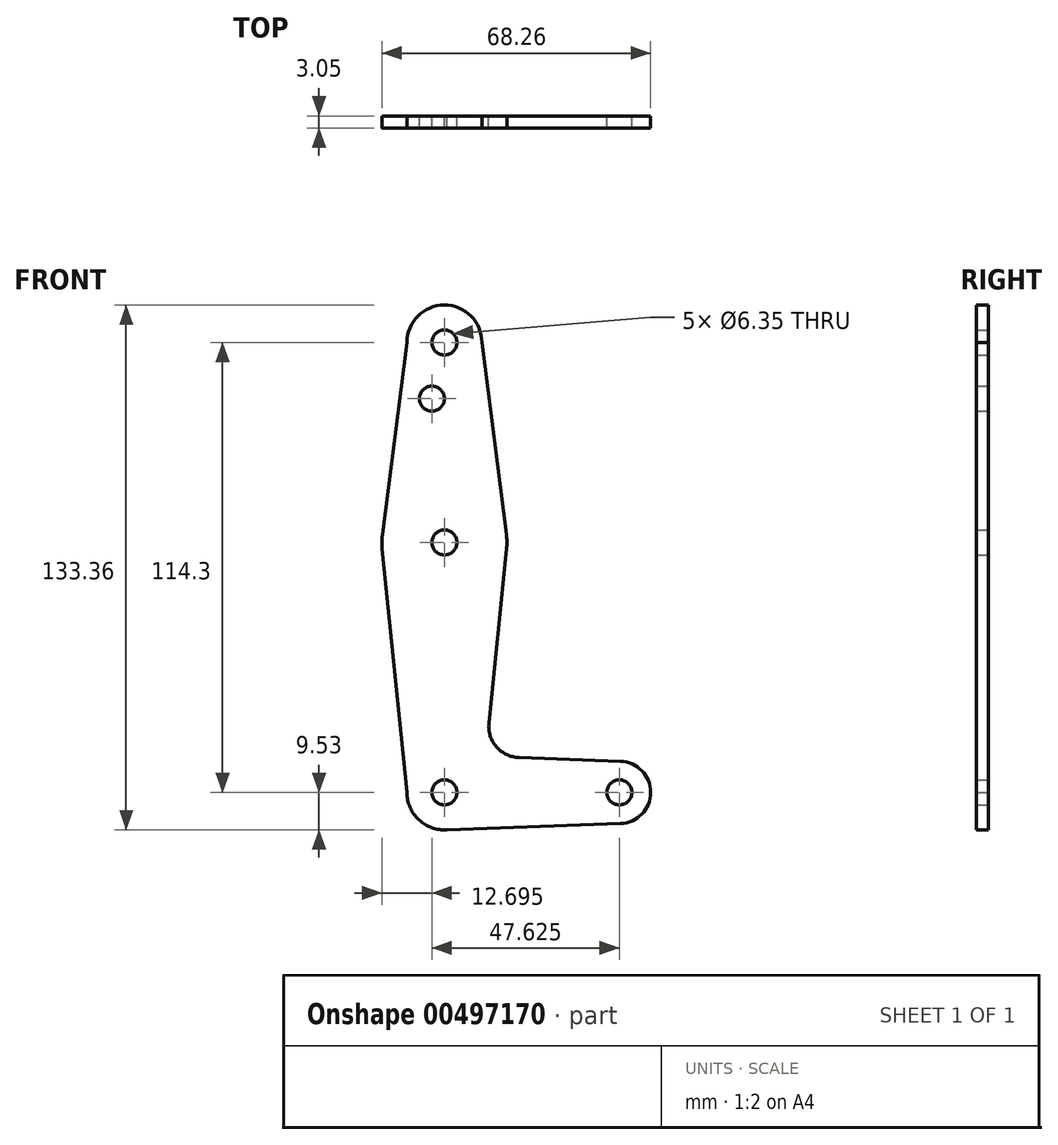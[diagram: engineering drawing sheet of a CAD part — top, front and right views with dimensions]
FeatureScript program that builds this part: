
annotation { "Feature Type Name" : "Feature", "Feature Type Description" : "" }
export const myFeature = defineFeature(function(context is Context, id is Id, definition is map)
    precondition{}
    {
        {
            var Q0;
            Q0=qCreatedBy(makeId("Front.planeOp"),FACE);
            var sketch = newSketch(context, id + "F0", { "sketchPlane" : qUnion([Q0])});
            skLineSegment(sketch, "E0", {"start": v(0, 0) * mm, "end": v(0, 114.3) * mm, "construction": true});
            skLineSegment(sketch, "E1", {"start": v(0, 0) * mm, "end": v(44.45, 0) * mm, "construction": true});
            skCircle(sketch, "E2", {"center": v(0, 0) * mm, "radius": 9.53 * mm});
            skCircle(sketch, "E3", {"center": v(44.45, 0) * mm, "radius": 7.94 * mm});
            skCircle(sketch, "E4", {"center": v(0, 63.5) * mm, "radius": 15.88 * mm});
            skCircle(sketch, "E5", {"center": v(0, 114.3) * mm, "radius": 9.53 * mm});
            skLineSegment(sketch, "E6", {"start": v(9.53, 114.3) * mm, "end": v(15.75, 65.5) * mm});
            skLineSegment(sketch, "E7", {"start": v(-9.52, 114.3) * mm, "end": v(-15.75, 65.5) * mm});
            skLineSegment(sketch, "E8", {"start": v(-15.8, 61.9) * mm, "end": v(-9.52, 0) * mm});
            skLineSegment(sketch, "E9", {"start": v(15.8, 61.9) * mm, "end": v(11.3, 17.6) * mm});
            skLineSegment(sketch, "E10", {"start": v(18.93, 8.85) * mm, "end": v(44.73, 7.93) * mm});
            skLineSegment(sketch, "E11", {"start": v(0, -9.53) * mm, "end": v(44.73, -7.93) * mm});
            skCircle(sketch, "E12", {"center": v(0, 114.3) * mm, "radius": 3.18 * mm});
            skCircle(sketch, "E13", {"center": v(0, 63.5) * mm, "radius": 3.18 * mm});
            skCircle(sketch, "E14", {"center": v(0, 0) * mm, "radius": 3.18 * mm});
            skCircle(sketch, "E15", {"center": v(44.45, 0) * mm, "radius": 3.18 * mm});
            skCircle(sketch, "E16", {"center": v(-3.18, 100.03) * mm, "radius": 3.18 * mm});
            skArc(sketch, "E17.filletArc", {"start": v(11.3, 17.6) * mm, "mid": v(13.22, 11.57) * mm, "end": v(18.93, 8.85) * mm});
            skSolve(sketch);
        }
        {
            var Q0;
            Q0 = qSketchRegion(id + "F0", true);
            extrude(context, id + "F1", {"entities" : qUnion([Q0]), "depth" : 3.05 * mm});
        }
    });
